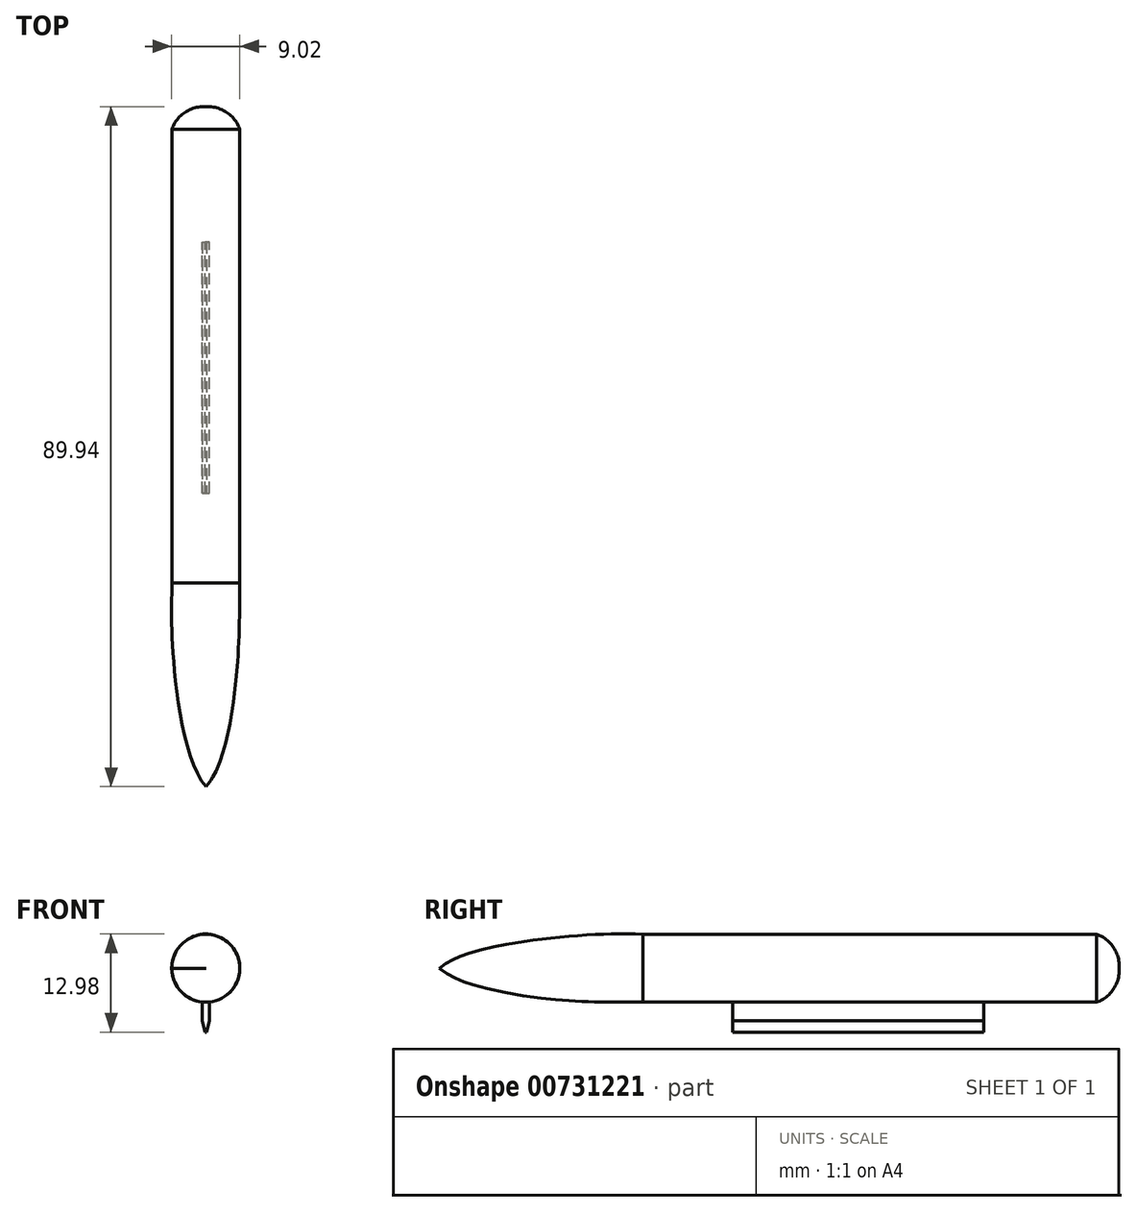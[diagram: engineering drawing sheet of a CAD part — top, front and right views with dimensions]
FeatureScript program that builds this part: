
annotation { "Feature Type Name" : "Feature", "Feature Type Description" : "" }
export const myFeature = defineFeature(function(context is Context, id is Id, definition is map)
    precondition{}
    {
        {
            var Q0;
            Q0=qCreatedBy(makeId("Front.planeOp"),FACE);
            var sketch = newSketch(context, id + "F0", { "sketchPlane" : qUnion([Q0])});
            skCircle(sketch, "E0", {"center": v(0, 0) * mm, "radius": 4.5 * mm});
            skSolve(sketch);
        }
        {
            var Q0;
            Q0=qCreatedBy(makeId("Front.planeOp"),FACE);
            cPlane(context, id + "F1", {"entities" : qUnion([Q0]), "cplaneType" : CPlaneType.OFFSET, "offset" : 60 * mm, "width" : 150 * mm, "height" : 150 * mm});
        }
        {
            var Q0;
            Q0=qCreatedBy(id+"F1.planeOp",FACE);
            var sketch = newSketch(context, id + "F2", { "sketchPlane" : qUnion([Q0])});
            skCircle(sketch, "E1", {"center": v(0, 0) * mm, "radius": 4.5 * mm});
            skSolve(sketch);
        }
        {
            var Q0;
            Q0=sQuery(id+"F0.wireOp",EDGE,"E0");
            extrude(context, id + "F3", {"bodyType" : ToolBodyType.SURFACE, "surfaceEntities" : qUnion([Q0]), "depth" : 60 * mm, "offsetDistance" : 25 * mm});
        }
        {
            var Q0;
            Q0=makeQuery(id+"F2.imprint","IMPRINT",FACE,{"disambiguationData":[TD([[makeQuery(id+"F2.imprint","IMPRINT",EDGE,{"derivedFrom":sQuery(id+"F2.wireOp",EDGE,"E1")}),1.0]])]});
            var sketch = newSketch(context, id + "F4", { "sketchPlane" : qUnion([Q0])});
            skPoint(sketch, "E2", {"position": v(4.5, 0) * mm});
            skPoint(sketch, "E3", {"position": v(-4.5, 0) * mm});
            skPoint(sketch, "E4", {"position": v(0, -4.5) * mm});
            skPoint(sketch, "E5", {"position": v(0, 4.5) * mm});
            skSolve(sketch);
        }
        {
            var Q0;
            Q0=qCreatedBy(makeId("Top.planeOp"),FACE);
            var sketch = newSketch(context, id + "F5", { "sketchPlane" : qUnion([Q0])});
            skFitSpline(sketch, "E6", {"points": [v(-4.5, -60) * mm, v(-4.23, -70.61) * mm, v(0, -86.94) * mm], "startDerivative": vector(-0.08, -29.66) * mm, "endDerivative": vector(14.32, -16.3) * mm});
            skFitSpline(sketch, "E7", {"points": [v(0, -86.94) * mm, v(4.19, -70.68) * mm, v(4.5, -60) * mm], "startDerivative": vector(15.12, 16.21) * mm, "endDerivative": vector(0.48, 29.25) * mm});
            skSolve(sketch);
        }
        {
            var Q0;
            Q0=qCreatedBy(makeId("Right.planeOp"),FACE);
            var sketch = newSketch(context, id + "F6", { "sketchPlane" : qUnion([Q0])});
            skFitSpline(sketch, "E8", {"points": [v(-60, -4.5) * mm, v(-70.65, -4.22) * mm, v(-86.94, 0) * mm], "startDerivative": vector(-34.6, 0.4) * mm, "endDerivative": vector(-15.88, 14.42) * mm});
            skFitSpline(sketch, "E9", {"points": [v(-86.94, 0) * mm, v(-70.62, 4.12) * mm, v(-60, 4.5) * mm], "startDerivative": vector(16.22, 14.34) * mm, "endDerivative": vector(34, -0.55) * mm});
            skSolve(sketch);
        }
        {
            var Q0;
            Q0=makeQuery(id+"F2.imprint","IMPRINT",FACE,{"disambiguationData":[TD([[makeQuery(id+"F2.imprint","IMPRINT",EDGE,{"derivedFrom":sQuery(id+"F2.wireOp",EDGE,"E1")}),1.0]])]});
            var Q1;
            Q1=sQuery(id+"F6.wireOp",VERTEX,"E9.0.internal");
            var Q2;
            Q2=sQuery(id+"F5.wireOp",EDGE,"E6");
            var Q3;
            Q3=sQuery(id+"F5.wireOp",EDGE,"E7");
            var Q4;
            Q4=sQuery(id+"F6.wireOp",EDGE,"E8");
            var Q5;
            Q5=sQuery(id+"F6.wireOp",EDGE,"E9");
            loft(context, id + "F7", {"addGuides" : true, "sheetProfilesArray" : [{ "sheetProfileEntities" : qUnion([Q0]) }, { "sheetProfileEntities" : qUnion([Q1]) }], "guidesArray" : [{ "guideEntities" : qUnion([Q2]), "guideDerivativeType" : LoftGuideDerivativeType.DEFAULT, "guideDerivativeMagnitude" : 1 }, { "guideEntities" : qUnion([Q3]), "guideDerivativeType" : LoftGuideDerivativeType.DEFAULT, "guideDerivativeMagnitude" : 1 }, { "guideEntities" : qUnion([Q4]), "guideDerivativeType" : LoftGuideDerivativeType.DEFAULT, "guideDerivativeMagnitude" : 1 }, { "guideEntities" : qUnion([Q5]), "guideDerivativeType" : LoftGuideDerivativeType.DEFAULT, "guideDerivativeMagnitude" : 1 }]});
        }
        {
            var Q0;
            Q0=qCreatedBy(makeId("Right.planeOp"),FACE);
            var sketch = newSketch(context, id + "F8", { "sketchPlane" : qUnion([Q0])});
            skLineSegment(sketch, "E10.bottom", {"start": v(-48.13, -4.44) * mm, "end": v(-14.9, -4.45) * mm});
            skLineSegment(sketch, "E10.top", {"start": v(-48.13, -8.44) * mm, "end": v(-14.93, -8.45) * mm});
            skLineSegment(sketch, "E10.left", {"start": v(-48.13, -8.44) * mm, "end": v(-48.13, -4.44) * mm});
            skLineSegment(sketch, "E10.right", {"start": v(-14.93, -8.45) * mm, "end": v(-14.9, -4.45) * mm});
            skSolve(sketch);
        }
        {
            var Q0;
            Q0=makeQuery(id+"F8.imprint","IMPRINT",FACE,{"disambiguationData":[TD([[makeQuery(id+"F8.imprint","IMPRINT",EDGE,{"derivedFrom":sQuery(id+"F8.wireOp",EDGE,"E10.bottom")}),-1.0]])]});
            extrude(context, id + "F9", {"entities" : qUnion([Q0]), "endBound" : BoundingType.SYMMETRIC, "depth" : 1 * mm, "offsetDistance" : 25 * mm});
        }
        {
            var Q0;
            Q0=makeQuery(id+"F9.opExtrude","CAP_EDGE",EDGE,{"disambiguationData":[OSD([sQuery(id+"F8.wireOp",EDGE,"E10.top")])],"isStart":false});
            var Q1;
            Q1=makeQuery(id+"F9.opExtrude","CAP_EDGE",EDGE,{"disambiguationData":[OSD([sQuery(id+"F8.wireOp",EDGE,"E10.top")])],"isStart":true});
            chamfer(context, id + "F10", {"entities" : qUnion([Q0, Q1]), "chamferType" : ChamferType.OFFSET_ANGLE, "width" : 1.5 * mm, "oppositeDirection" : false, "angle" : 15 * degree, "tangentPropagation" : true});
        }
        {
            var Q0;
            Q0=makeQuery(id+"FlL8xsbAWAlsFt4_0.boolean.opBoolean","MERGE",FACE,{"derivedFrom":[makeQuery(id+"F9.opExtrude","SWEPT_FACE",FACE,{"disambiguationData":[OSD([sQuery(id+"F8.wireOp",EDGE,"E10.right")])]}),makeQuery(id+"FlL8xsbAWAlsFt4_0.opExtrude","CAP_FACE",FACE,{"disambiguationData":[OSD([sQuery(id+"F0.wireOp",EDGE,"E0")])],"isStart":true})]});
            var sketch = newSketch(context, id + "F11", { "sketchPlane" : qUnion([Q0])});
            skCircle(sketch, "E11", {"center": v(0, 0) * mm, "radius": 3 * mm});
            skSolve(sketch);
        }
        {
            var Q0;
            Q0=makeQuery(id+"F0.imprint","IMPRINT",FACE,{"disambiguationData":[TD([[makeQuery(id+"F0.imprint","IMPRINT",EDGE,{"derivedFrom":sQuery(id+"F0.wireOp",EDGE,"E0")}),1.0]])]});
            extrude(context, id + "F12", {"entities" : qUnion([Q0]), "operationType" : NewBodyOperationType.ADD, "depth" : 60 * mm, "offsetDistance" : 25 * mm});
        }
        {
            var Q0;
            Q0=makeQuery(id+"F12.opExtrude","CAP_FACE",FACE,{"disambiguationData":[OSD([sQuery(id+"F0.wireOp",EDGE,"E0")])],"isStart":true});
            extrude(context, id + "F13", {"entities" : qUnion([Q0]), "depth" : 3 * mm, "offsetDistance" : 25 * mm});
        }
        {
            var Q0;
            Q0=makeQuery(id+"F13.opExtrude","CAP_FACE",FACE,{"disambiguationData":[OSD([sQuery(id+"F0.wireOp",EDGE,"E0")])],"isStart":false});
            var Q1;
            Q1=makeQuery(id+"F13.opExtrude","CAP_FACE",FACE,{"disambiguationData":[OSD([sQuery(id+"F11.wireOp",EDGE,"E11")])],"isStart":false});
            fillet(context, id + "F14", {"entities" : qUnion([Q0, Q1]), "radius" : 4.5 * mm, "tangentPropagation" : true, "allowEdgeOverflow" : false});
        }
    });
